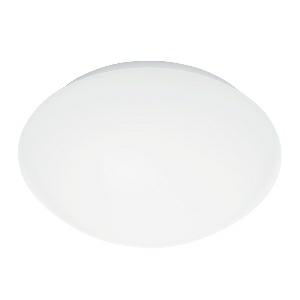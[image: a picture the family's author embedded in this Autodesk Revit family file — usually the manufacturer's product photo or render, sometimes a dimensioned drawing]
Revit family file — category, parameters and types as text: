
# Revit family: rs_pro_led_p2_sl_056094
name_source: partatom
category: Leuchten
revit_build: Autodesk Revit 2016 (Build: 20190508_0715(x64)
units: mm (PartAtom-declared; Revit-internal decimal feet)

## family parameters
Basisbauteil = Fläche
Beim Laden mit Abzugskörper schneiden = Nein
Bemaßung runder Anschluss = Durchmesser verwenden
Gemeinsam genutzt = Nein
Lichtquelle = Nein
Raumberechnungspunkt = Nein
Teiletyp = Normal

## types (1)
- RS PRO LED P2 SL (1 x , 1730 lm, 3000 K)
    Beschreibung = Dimensions (Ø x H): 320 x 110 mm; Mains power supply: 220 – 240 V / 50 – 60 Hz; Output: 15,5 W; Luminous flux: 1730 lm; Colour temperature: 3000 K; Colour variation LED: SDCM3; Colour Rendering Index CRI: 80-89; With lamp: Yes, STEINEL LED system; Lamp: LED cannot be replaced; LED life expectancy (max. °C): 50000 h; Drop in luminous flux in accordance with LM80: L80B10; Base: without; LED cooling system: Passive Thermo Control; With motion detector: No; Photo-cell controller: No; Basic light level function: No; Soft light start: Yes; Impact resistance: IK03; IP-rating: IP54; Protection class: II; Ambient temperature: 10 – 40 °C; Housing material: Plastic; Cover material: Plastic, opal; Manufacturer's Warranty: 5 years; With remote control: No; Version: warm white; PU1, EAN: 4007841056094
    CIE Flux Codes = 39 68 87 86 100
    Color Rendering = 80-89
    Color Temperature = 3000 K
    Frequency = 60 Hz, 50 Hz
    Height = 0 mm  [stored 0 ft]
    Hersteller = Steinel
    Lamp Light Flux = 1730 lm
    Lamp count = 1
    Lampe = 1 x
    Length = 320 mm
    Luminous efficacy = 115 lm/W
    ModVariant = Nein
    Modell = 056094
    Mounting Type = Surface mounted
    Number of Poles = 1
    OnlyDefault = Ja
    Power Factor = 1
    Product Name = RS PRO LED P2 SL
    Product group = Sensor-switched indoor light
    ProductGroupID = 30
    Protection Class = Protection class II
    Protection Degree = IP 54
    RlxData = <blob elided: 35849 chars, md5=96415d94>
    Scheinlast = 15 VA
    Socket = socket
    Standby Power = 0 W
    System Light Flux = 1730 lm
    System Power = 15 W
    Typenbild = produkt1_056094.jpg
    Typenkommentare = Product without accessories
    URL = http://relux.com
    VarID = ---
    Voltage = 0 V
    Vorgabe-Ansicht = 1800 mm
    Weight = 0.00 kg
    Width = 0 mm  [stored 0 ft]

note: [stored X ft] marks values corroborated as IEEE doubles in the binary element streams (Revit-internal decimal feet)

## geometry (parser evidence)
native form markers: Sweep x13
no freeform markers — native parametric forms only
